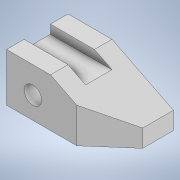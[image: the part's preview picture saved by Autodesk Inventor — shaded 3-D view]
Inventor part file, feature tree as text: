
AUTODESK INVENTOR PART (.ipt)
format: ipt  version: 2022.2 (Build 262287030, 287C)  size: 139,776 bytes
history: native  units: in
note: dims shown in document units (in); Inventor stores cm internally (conversion verified against a paired STEP export)
features: sketch x5, extrude x4, hole x1, projected_geometry x1
ambient origin geometry x8: Origin, YZ Plane, XZ Plane, XY Plane, X Axis, Y Axis, Z Axis, Center Point
bodies: Solid1 (feature_tree)
feature tree (11):
  extrude  "Extrusion1"  Depth=2.75in
  extrude  "Extrusion3"  Depth=1.5in
  extrude  "Extrusion4"  Depth=0.5in
  extrude  "Extrusion5"  TaperAngle=0.0deg  [1 undecoded]
  hole  "Hole1"  [1 undecoded]
  sketch  "Sketch1"  dims[d0=3.5in d1=2.75in]
  sketch  "Sketch4"  dims[d2=6.0in d3=0.0in d6=1.5in]
  sketch  "Sketch5"  dims[d7=1.0in d8=0.5in]
  projected_geometry  "Projected Loop1"
  sketch  "Sketch6"  dims[d9=0.0in d10=0.0in d19=0.0in d20=0.0in]
  sketch  "Sketch8"  dims[d22=4.0in d26=0.0in d27=0.0in d28=1.0in d29=2.5in d30=1.75in d31=1.5in d32=1.25in d33=1.0in d34=0.75in d35=0.375in d36=0.25in d37=0.5635in d38=1.0in d39=0.8108in]
note: 2 required parameter values undecoded (feature->parameter linkage not recoverable at this tier; creation-order binding heuristic only, values carry confidence <= 0.55)
